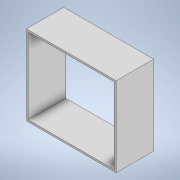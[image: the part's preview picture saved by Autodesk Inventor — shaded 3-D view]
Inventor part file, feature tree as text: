
AUTODESK INVENTOR PART (.ipt)
format: ipt  version: 2021 (Build 250183000, 183)  size: 100,864 bytes
history: native  units: mm
features: extrude x1, sketch x1
ambient origin geometry x8: Origin, YZ Plane, XZ Plane, XY Plane, X Axis, Y Axis, Z Axis, Center Point
bodies: Solid1 (feature_tree)
feature tree (2):
  extrude  "Extrusion1"  Depth=81.2mm
  sketch  "Sketch1"  dims[d0=92.0mm d1=81.2mm d2=40.6mm d3=40.6mm d4=2.0mm d5=2.0mm d6=2.0mm d7=2.0mm d8=40.0mm d9=0.0mm]
